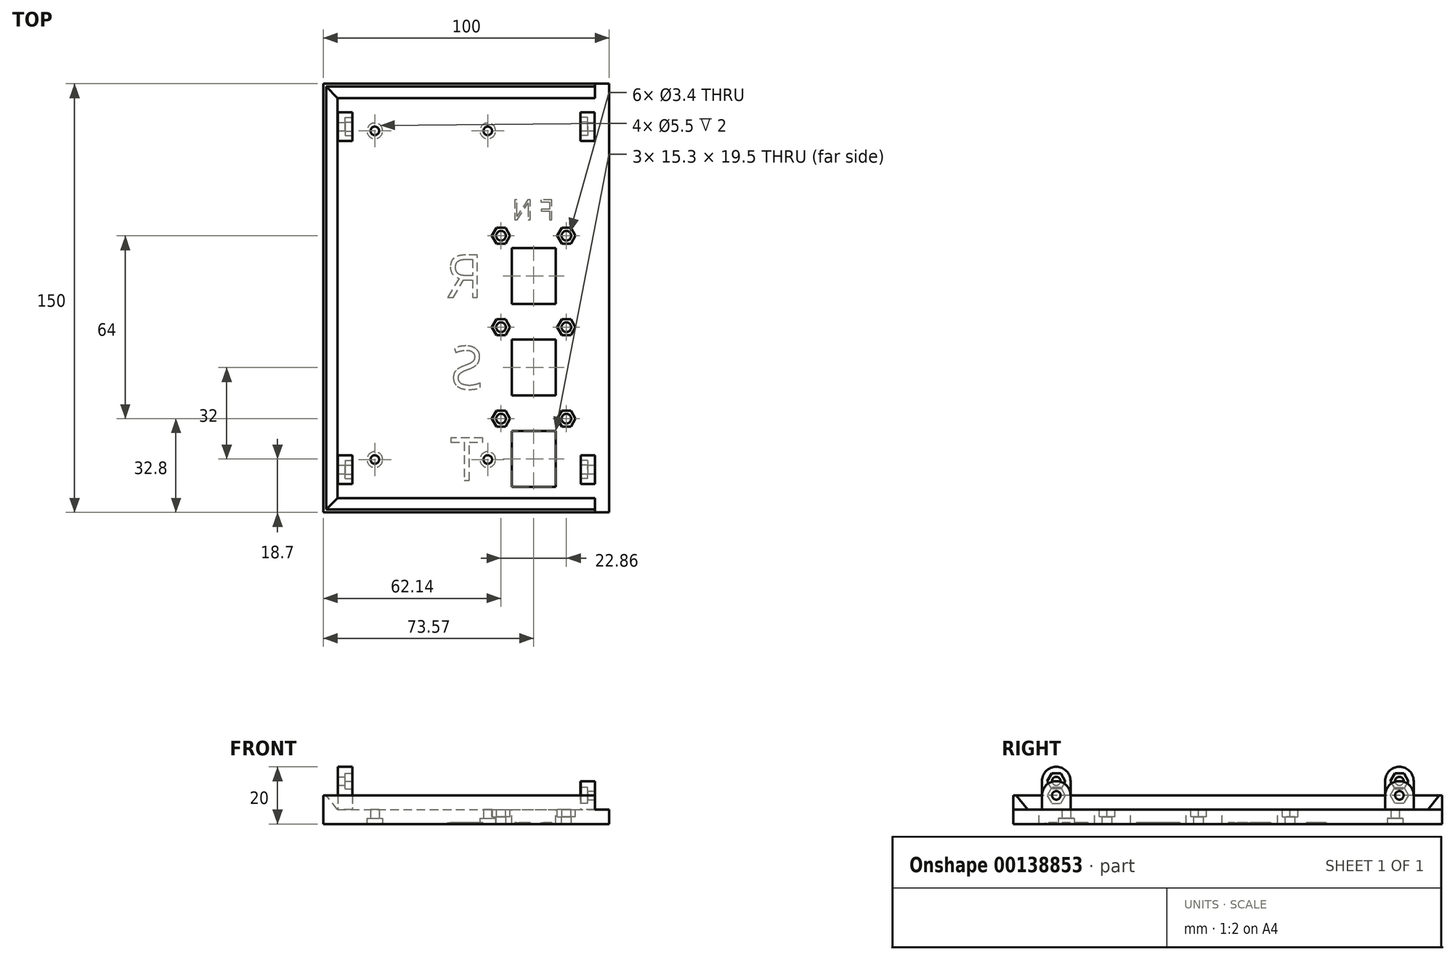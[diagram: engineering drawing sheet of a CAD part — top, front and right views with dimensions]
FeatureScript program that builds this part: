
annotation { "Feature Type Name" : "Feature", "Feature Type Description" : "" }
export const myFeature = defineFeature(function(context is Context, id is Id, definition is map)
    precondition{}
    {
        {
            var Q0;
            Q0=qCreatedBy(makeId("Top.planeOp"),FACE);
            var sketch = newSketch(context, id + "F0", { "sketchPlane" : qUnion([Q0])});
            skLineSegment(sketch, "E0.bottom", {"start": v(50, 75) * mm, "end": v(-50, 75) * mm});
            skLineSegment(sketch, "E0.top", {"start": v(50, -75) * mm, "end": v(-50, -75) * mm});
            skLineSegment(sketch, "E0.left", {"start": v(50, 75) * mm, "end": v(50, -75) * mm});
            skLineSegment(sketch, "E0.right", {"start": v(-50, 75) * mm, "end": v(-50, -75) * mm});
            skPoint(sketch, "E0.middle", {"position": v(0, 0) * mm});
            skSolve(sketch);
        }
        {
            var Q0;
            Q0 = qSketchRegion(id + "F0", true);
            extrude(context, id + "F1", {"entities" : qUnion([Q0]), "depth" : 5 * mm});
        }
        {
            var Q0;
            Q0=makeQuery(id+"F1.opExtrude","CAP_FACE",FACE,{"disambiguationData":[OSD([sQuery(id+"F0.wireOp",EDGE,"E0.bottom"),sQuery(id+"F0.wireOp",EDGE,"E0.top"),sQuery(id+"F0.wireOp",EDGE,"E0.left"),sQuery(id+"F0.wireOp",EDGE,"E0.right")])],"isStart":false});
            var sketch = newSketch(context, id + "F2", { "sketchPlane" : qUnion([Q0])});
            skLineSegment(sketch, "E1.bottom", {"start": v(-50, 75) * mm, "end": v(50, 75) * mm});
            skLineSegment(sketch, "E1.top", {"start": v(-50, -75) * mm, "end": v(50, -75) * mm});
            skLineSegment(sketch, "E1.left", {"start": v(-50, 75) * mm, "end": v(-50, -75) * mm});
            skLineSegment(sketch, "E1.right", {"start": v(50, 75) * mm, "end": v(50, -75) * mm});
            skLineSegment(sketch, "E2.bottom", {"start": v(-45, 70) * mm, "end": v(45, 70) * mm});
            skLineSegment(sketch, "E2.top", {"start": v(-45, -70) * mm, "end": v(45, -70) * mm});
            skLineSegment(sketch, "E2.left", {"start": v(-45, 70) * mm, "end": v(-45, -70) * mm});
            skLineSegment(sketch, "E2.right", {"start": v(45, 70) * mm, "end": v(45, -70) * mm});
            skLineSegment(sketch, "E3", {"start": v(45, 70) * mm, "end": v(45, 75) * mm});
            skLineSegment(sketch, "E4", {"start": v(45, -70) * mm, "end": v(45, -75) * mm});
            skSolve(sketch);
        }
        {
            var Q0;
            Q0=makeQuery(id+"FjEDbnMBrPMrPUJ_1.boolean.opBoolean","MERGE",FACE,{"derivedFrom":[makeQuery(id+"F1.opExtrude","SWEPT_FACE",FACE,{"disambiguationData":[OSD([sQuery(id+"F0.wireOp",EDGE,"E0.top")])]}),makeQuery(id+"FjEDbnMBrPMrPUJ_1.opExtrude","SWEPT_FACE",FACE,{"disambiguationData":[OSD([sQuery(id+"F2.wireOp",EDGE,"E1.top")])]})]});
            var sketch = newSketch(context, id + "F3", { "sketchPlane" : qUnion([Q0])});
            skLineSegment(sketch, "E5", {"start": v(-50, 0) * mm, "end": v(-50, 10) * mm});
            skLineSegment(sketch, "E6", {"start": v(-50, 10) * mm, "end": v(-49, 10) * mm});
            skLineSegment(sketch, "E7", {"start": v(-50, 5) * mm, "end": v(-45, 5) * mm});
            skLineSegment(sketch, "E8", {"start": v(-49, 10) * mm, "end": v(-45, 5) * mm});
            skSolve(sketch);
        }
        {
            var Q0;
            Q0=makeQuery(id+"F1.opExtrude","SWEPT_FACE",FACE,{"disambiguationData":[OSD([sQuery(id+"F0.wireOp",EDGE,"E0.left")])]});
            var sketch = newSketch(context, id + "F4", { "sketchPlane" : qUnion([Q0])});
            skLineSegment(sketch, "E9", {"start": v(-75, 0) * mm, "end": v(-75, 10) * mm});
            skLineSegment(sketch, "E10", {"start": v(-75, 5) * mm, "end": v(-70, 5) * mm});
            skLineSegment(sketch, "E11", {"start": v(-75, 10) * mm, "end": v(-74, 10) * mm});
            skLineSegment(sketch, "E12", {"start": v(-74, 10) * mm, "end": v(-70, 5) * mm});
            skLineSegment(sketch, "E13.MirrorCS", {"start": v(75, 10) * mm, "end": v(74, 10) * mm});
            skLineSegment(sketch, "E14.MirrorCS", {"start": v(75, 0) * mm, "end": v(75, 10) * mm});
            skLineSegment(sketch, "E15.MirrorCS", {"start": v(75, 5) * mm, "end": v(70, 5) * mm});
            skLineSegment(sketch, "E16.MirrorCS", {"start": v(74, 10) * mm, "end": v(70, 5) * mm});
            skSolve(sketch);
        }
        {
            var Q0;
            Q0 = qSketchRegion(id + "F3", true);
            extrude(context, id + "F5", {"entities" : qUnion([Q0]), "operationType" : NewBodyOperationType.ADD, "oppositeDirection" : true, "depth" : 150 * mm});
        }
        {
            var Q0;
            Q0 = qSketchRegion(id + "F4", true);
            extrude(context, id + "F6", {"entities" : qUnion([Q0]), "operationType" : NewBodyOperationType.ADD, "oppositeDirection" : true, "depth" : 100 * mm});
        }
        {
            var Q0;
            Q0=makeQuery(id+"F6.boolean.opBoolean","MERGE",FACE,{"derivedFrom":[makeQuery(id+"F5.boolean.opBoolean","MERGE",FACE,{"derivedFrom":[makeQuery(id+"F1.opExtrude","SWEPT_FACE",FACE,{"disambiguationData":[OSD([sQuery(id+"F0.wireOp",EDGE,"E0.top")])]}),makeQuery(id+"F5.opExtrude","CAP_FACE",FACE,{"disambiguationData":[OSD([sQuery(id+"F3.wireOp",EDGE,"E5"),sQuery(id+"F3.wireOp",EDGE,"E6"),sQuery(id+"F3.wireOp",EDGE,"E7"),sQuery(id+"F3.wireOp",EDGE,"E8")])],"isStart":true})]}),makeQuery(id+"F6.opExtrude","SWEPT_FACE",FACE,{"disambiguationData":[OSD([sQuery(id+"F4.wireOp",EDGE,"E9")])]})]});
            var sketch = newSketch(context, id + "F7", { "sketchPlane" : qUnion([Q0])});
            skLineSegment(sketch, "E17.bottom", {"start": v(50, 10) * mm, "end": v(45, 10) * mm});
            skLineSegment(sketch, "E17.top", {"start": v(50, 5) * mm, "end": v(45, 5) * mm});
            skLineSegment(sketch, "E17.left", {"start": v(50, 10) * mm, "end": v(50, 5) * mm});
            skLineSegment(sketch, "E17.right", {"start": v(45, 10) * mm, "end": v(45, 5) * mm});
            skSolve(sketch);
        }
        {
            var Q0;
            Q0 = qSketchRegion(id + "F7", true);
            extrude(context, id + "F8", {"entities" : qUnion([Q0]), "operationType" : NewBodyOperationType.REMOVE, "oppositeDirection" : true, "depth" : 160 * mm});
        }
        {
            var Q0;
            Q0=makeQuery(id+"F8.boolean.opBoolean","MERGE",FACE,{"derivedFrom":[makeQuery(id+"F1.opExtrude","CAP_FACE",FACE,{"disambiguationData":[OSD([sQuery(id+"F0.wireOp",EDGE,"E0.bottom"),sQuery(id+"F0.wireOp",EDGE,"E0.top"),sQuery(id+"F0.wireOp",EDGE,"E0.left"),sQuery(id+"F0.wireOp",EDGE,"E0.right")])],"isStart":false}),makeQuery(id+"F8.opExtrude","SWEPT_FACE",FACE,{"disambiguationData":[OSD([sQuery(id+"F7.wireOp",EDGE,"E17.top")])]})]});
            var sketch = newSketch(context, id + "F9", { "sketchPlane" : qUnion([Q0])});
            skLineSegment(sketch, "E18.bottom", {"start": v(15.92, 17.45) * mm, "end": v(31.22, 17.45) * mm});
            skLineSegment(sketch, "E18.top", {"start": v(15.92, -2.05) * mm, "end": v(31.22, -2.05) * mm});
            skLineSegment(sketch, "E18.left", {"start": v(15.92, 17.45) * mm, "end": v(15.92, -2.05) * mm});
            skLineSegment(sketch, "E18.right", {"start": v(31.22, 17.45) * mm, "end": v(31.22, -2.05) * mm});
            skLineSegment(sketch, "E19.bottom", {"start": v(5.14, 26) * mm, "end": v(42, 26) * mm});
            skLineSegment(sketch, "E19.left", {"start": v(5.14, 26) * mm, "end": v(5.14, -4.5) * mm});
            skLineSegment(sketch, "E19.right", {"start": v(42, 26) * mm, "end": v(42, -4.5) * mm});
            skCircle(sketch, "E20", {"center": v(12.14, 21.8) * mm, "radius": 1.7 * mm});
            skCircle(sketch, "E21", {"center": v(35, 21.8) * mm, "radius": 1.7 * mm});
            skLineSegment(sketch, "E22", {"start": v(5.14, -4.5) * mm, "end": v(42, -4.5) * mm});
            skLineSegment(sketch, "E23.0.1.0", {"start": v(5.14, -6) * mm, "end": v(42, -6) * mm});
            skLineSegment(sketch, "E23.0.1.1", {"start": v(15.92, -14.55) * mm, "end": v(31.22, -14.55) * mm});
            skLineSegment(sketch, "E23.0.1.2", {"start": v(5.14, -36.5) * mm, "end": v(42, -36.5) * mm});
            skLineSegment(sketch, "E23.0.1.3", {"start": v(31.22, -14.55) * mm, "end": v(31.22, -34.05) * mm});
            skLineSegment(sketch, "E23.0.1.4", {"start": v(42, -6) * mm, "end": v(42, -36.5) * mm});
            skLineSegment(sketch, "E23.0.1.5", {"start": v(15.92, -14.55) * mm, "end": v(15.92, -34.05) * mm});
            skLineSegment(sketch, "E23.0.1.6", {"start": v(5.14, -6) * mm, "end": v(5.14, -36.5) * mm});
            skLineSegment(sketch, "E23.0.1.7", {"start": v(15.92, -34.05) * mm, "end": v(31.22, -34.05) * mm});
            skCircle(sketch, "E23.0.1.8", {"center": v(35, -10.2) * mm, "radius": 1.7 * mm});
            skCircle(sketch, "E23.0.1.9", {"center": v(12.14, -10.2) * mm, "radius": 1.7 * mm});
            skLineSegment(sketch, "E23.0.2.0", {"start": v(5.14, -38) * mm, "end": v(42, -38) * mm});
            skLineSegment(sketch, "E23.0.2.1", {"start": v(15.92, -46.55) * mm, "end": v(31.22, -46.55) * mm});
            skLineSegment(sketch, "E23.0.2.2", {"start": v(5.14, -68.5) * mm, "end": v(42, -68.5) * mm});
            skLineSegment(sketch, "E23.0.2.3", {"start": v(31.22, -46.55) * mm, "end": v(31.22, -66.05) * mm});
            skLineSegment(sketch, "E23.0.2.4", {"start": v(42, -38) * mm, "end": v(42, -68.5) * mm});
            skLineSegment(sketch, "E23.0.2.5", {"start": v(15.92, -46.55) * mm, "end": v(15.92, -66.05) * mm});
            skLineSegment(sketch, "E23.0.2.6", {"start": v(5.14, -38) * mm, "end": v(5.14, -68.5) * mm});
            skLineSegment(sketch, "E23.0.2.7", {"start": v(15.92, -66.05) * mm, "end": v(31.22, -66.05) * mm});
            skCircle(sketch, "E23.0.2.8", {"center": v(35, -42.2) * mm, "radius": 1.7 * mm});
            skCircle(sketch, "E23.0.2.9", {"center": v(12.14, -42.2) * mm, "radius": 1.7 * mm});
            skLineSegment(sketch, "E23.direction1", {"start": v(5.14, -4.5) * mm, "end": v(42, -4.5) * mm, "construction": true});
            skLineSegment(sketch, "E23.direction2", {"start": v(5.14, -4.5) * mm, "end": v(5.14, -36.5) * mm, "construction": true});
            skSolve(sketch);
        }
        {
            var Q0;
            Q0=makeQuery(id+"F1.opExtrude","CAP_FACE",FACE,{"disambiguationData":[OSD([sQuery(id+"F0.wireOp",EDGE,"E0.bottom"),sQuery(id+"F0.wireOp",EDGE,"E0.top"),sQuery(id+"F0.wireOp",EDGE,"E0.left"),sQuery(id+"F0.wireOp",EDGE,"E0.right")])],"isStart":true});
            var sketch = newSketch(context, id + "F10", { "sketchPlane" : qUnion([Q0])});
            skCircle(sketch, "E24", {"center": v(7.5, 56.5) * mm, "radius": 1.5 * mm});
            skCircle(sketch, "E25", {"center": v(-32, -58.5) * mm, "radius": 1.5 * mm});
            skCircle(sketch, "E26", {"center": v(7.5, -58.5) * mm, "radius": 1.5 * mm});
            skCircle(sketch, "E27", {"center": v(-32, 56.5) * mm, "radius": 1.5 * mm});
            skSolve(sketch);
        }
        {
            var Q0;
            Q0 = qSketchRegion(id + "F10", true);
            extrude(context, id + "F11", {"entities" : qUnion([Q0]), "operationType" : NewBodyOperationType.REMOVE, "oppositeDirection" : true, "depth" : 25 * mm});
        }
        {
            var Q0;
            Q0=makeQuery(id+"F1.opExtrude","CAP_FACE",FACE,{"disambiguationData":[OSD([sQuery(id+"F0.wireOp",EDGE,"E0.bottom"),sQuery(id+"F0.wireOp",EDGE,"E0.top"),sQuery(id+"F0.wireOp",EDGE,"E0.left"),sQuery(id+"F0.wireOp",EDGE,"E0.right")])],"isStart":true});
            var sketch = newSketch(context, id + "F12", { "sketchPlane" : qUnion([Q0])});
            skCircle(sketch, "E28", {"center": v(-32, 56.5) * mm, "radius": 2.75 * mm});
            skCircle(sketch, "E29", {"center": v(7.5, 56.5) * mm, "radius": 2.75 * mm});
            skCircle(sketch, "E30", {"center": v(-32, -58.5) * mm, "radius": 2.75 * mm});
            skCircle(sketch, "E31", {"center": v(7.5, -58.5) * mm, "radius": 2.75 * mm});
            skSolve(sketch);
        }
        {
            var Q0;
            Q0 = qSketchRegion(id + "F12", true);
            extrude(context, id + "F13", {"entities" : qUnion([Q0]), "operationType" : NewBodyOperationType.REMOVE, "oppositeDirection" : true, "depth" : 2 * mm});
        }
        {
            var Q0;
            Q0=makeQuery(id+"F8.boolean.opBoolean","MERGE",FACE,{"derivedFrom":[makeQuery(id+"F1.opExtrude","CAP_FACE",FACE,{"disambiguationData":[OSD([sQuery(id+"F0.wireOp",EDGE,"E0.bottom"),sQuery(id+"F0.wireOp",EDGE,"E0.top"),sQuery(id+"F0.wireOp",EDGE,"E0.left"),sQuery(id+"F0.wireOp",EDGE,"E0.right")])],"isStart":false}),makeQuery(id+"F8.opExtrude","SWEPT_FACE",FACE,{"disambiguationData":[OSD([sQuery(id+"F7.wireOp",EDGE,"E17.top")])]})]});
            var sketch = newSketch(context, id + "F14", { "sketchPlane" : qUnion([Q0])});
            skLineSegment(sketch, "E32.bottom", {"start": v(-39.9, 65) * mm, "end": v(-44.9, 65) * mm});
            skLineSegment(sketch, "E32.top", {"start": v(-39.9, 55) * mm, "end": v(-44.9, 55) * mm});
            skLineSegment(sketch, "E32.left", {"start": v(-39.9, 65) * mm, "end": v(-39.9, 55) * mm});
            skLineSegment(sketch, "E32.right", {"start": v(-44.9, 65) * mm, "end": v(-44.9, 55) * mm});
            skLineSegment(sketch, "E33.bottom", {"start": v(44.9, 65) * mm, "end": v(39.9, 65) * mm});
            skLineSegment(sketch, "E33.top", {"start": v(44.9, 55) * mm, "end": v(39.9, 55) * mm});
            skLineSegment(sketch, "E33.left", {"start": v(44.9, 65) * mm, "end": v(44.9, 55) * mm});
            skLineSegment(sketch, "E33.right", {"start": v(39.9, 65) * mm, "end": v(39.9, 55) * mm});
            skLineSegment(sketch, "E34.bottom", {"start": v(-39.9, -55) * mm, "end": v(-44.9, -55) * mm});
            skLineSegment(sketch, "E34.top", {"start": v(-39.9, -65) * mm, "end": v(-44.9, -65) * mm});
            skLineSegment(sketch, "E34.left", {"start": v(-39.9, -55) * mm, "end": v(-39.9, -65) * mm});
            skLineSegment(sketch, "E34.right", {"start": v(-44.9, -55) * mm, "end": v(-44.9, -65) * mm});
            skLineSegment(sketch, "E35.bottom", {"start": v(45, -55) * mm, "end": v(40, -55) * mm});
            skLineSegment(sketch, "E35.top", {"start": v(45, -65) * mm, "end": v(40, -65) * mm});
            skLineSegment(sketch, "E35.left", {"start": v(45, -55) * mm, "end": v(45, -65) * mm});
            skLineSegment(sketch, "E35.right", {"start": v(40, -55) * mm, "end": v(40, -65) * mm});
            skSolve(sketch);
        }
        {
            var Q0;
            Q0 = qSketchRegion(id + "F14", true);
            extrude(context, id + "F15", {"entities" : qUnion([Q0]), "operationType" : NewBodyOperationType.ADD, "depth" : 20 * mm});
        }
        {
            var Q0;
            Q0=makeQuery(id+"F15.opExtrude","SWEPT_FACE",FACE,{"disambiguationData":[OSD([sQuery(id+"F14.wireOp",EDGE,"E35.left")])]});
            var sketch = newSketch(context, id + "F16", { "sketchPlane" : qUnion([Q0])});
            skCircle(sketch, "E36", {"center": v(-60, 10) * mm, "radius": 1.5 * mm});
            skLineSegment(sketch, "E37", {"start": v(-65, 10) * mm, "end": v(-65, 25) * mm});
            skLineSegment(sketch, "E38", {"start": v(-65, 25) * mm, "end": v(-55, 25) * mm});
            skLineSegment(sketch, "E39", {"start": v(-55, 25) * mm, "end": v(-55, 10) * mm});
            skArc(sketch, "E40", {"start": v(-55, 10) * mm, "mid": v(-60, 15) * mm, "end": v(-65, 10) * mm});
            skCircle(sketch, "E41.MirrorC", {"center": v(60, 10) * mm, "radius": 1.5 * mm});
            skLineSegment(sketch, "E42.MirrorCS", {"start": v(55, 25) * mm, "end": v(55, 10) * mm});
            skLineSegment(sketch, "E43.MirrorCS", {"start": v(65, 10) * mm, "end": v(65, 25) * mm});
            skArc(sketch, "E44.MirrorCS", {"start": v(55, 10) * mm, "mid": v(60, 15) * mm, "end": v(65, 10) * mm});
            skLineSegment(sketch, "E45.MirrorCS", {"start": v(65, 25) * mm, "end": v(55, 25) * mm});
            skSolve(sketch);
        }
        {
            var Q0;
            Q0 = qSketchRegion(id + "F16", true);
            extrude(context, id + "F17", {"entities" : qUnion([Q0]), "operationType" : NewBodyOperationType.REMOVE, "oppositeDirection" : true, "depth" : 10 * mm});
        }
        {
            var Q0;
            Q0=makeQuery(id+"F15.opExtrude","SWEPT_FACE",FACE,{"disambiguationData":[OSD([sQuery(id+"F14.wireOp",EDGE,"E34.left")])]});
            var sketch = newSketch(context, id + "F18", { "sketchPlane" : qUnion([Q0])});
            skCircle(sketch, "E46", {"center": v(-60, 15) * mm, "radius": 1.5 * mm});
            skArc(sketch, "E47", {"start": v(-55, 15) * mm, "mid": v(-60, 20) * mm, "end": v(-65, 15) * mm});
            skLineSegment(sketch, "E48", {"start": v(-55, 15) * mm, "end": v(-55, 25) * mm});
            skLineSegment(sketch, "E49", {"start": v(-55, 25) * mm, "end": v(-65, 25) * mm});
            skLineSegment(sketch, "E50", {"start": v(-65, 25) * mm, "end": v(-65, 15) * mm});
            skLineSegment(sketch, "E51.MirrorCS", {"start": v(55, 15) * mm, "end": v(55, 25) * mm});
            skLineSegment(sketch, "E52.MirrorCS", {"start": v(55, 25) * mm, "end": v(65, 25) * mm});
            skArc(sketch, "E53.MirrorCS", {"start": v(55, 15) * mm, "mid": v(60, 20) * mm, "end": v(65, 15) * mm});
            skLineSegment(sketch, "E54.MirrorCS", {"start": v(65, 25) * mm, "end": v(65, 15) * mm});
            skCircle(sketch, "E55.MirrorC", {"center": v(60, 15) * mm, "radius": 1.5 * mm});
            skSolve(sketch);
        }
        {
            var Q0;
            Q0 = qSketchRegion(id + "F18", true);
            extrude(context, id + "F19", {"entities" : qUnion([Q0]), "operationType" : NewBodyOperationType.REMOVE, "oppositeDirection" : true, "depth" : 25 * mm});
        }
        {
            var Q0;
            Q0=makeQuery(id+"F15.opExtrude","SWEPT_FACE",FACE,{"disambiguationData":[OSD([sQuery(id+"F14.wireOp",EDGE,"E35.right")])]});
            var sketch = newSketch(context, id + "F20", { "sketchPlane" : qUnion([Q0])});
            skCircle(sketch, "E56.cCircle", {"center": v(60, 10) * mm, "radius": 2.75 * mm, "construction": true});
            skLineSegment(sketch, "E56.0", {"start": v(58.41, 12.75) * mm, "end": v(61.59, 12.75) * mm});
            skLineSegment(sketch, "E56.1", {"start": v(61.59, 12.75) * mm, "end": v(63.18, 10) * mm});
            skLineSegment(sketch, "E56.2", {"start": v(63.18, 10) * mm, "end": v(61.59, 7.25) * mm});
            skLineSegment(sketch, "E56.3", {"start": v(61.59, 7.25) * mm, "end": v(58.41, 7.25) * mm});
            skLineSegment(sketch, "E56.4", {"start": v(58.41, 7.25) * mm, "end": v(56.82, 10) * mm});
            skLineSegment(sketch, "E56.5", {"start": v(56.82, 10) * mm, "end": v(58.41, 12.75) * mm});
            skPoint(sketch, "E56.0.midPoint", {"position": v(60, 12.75) * mm});
            skLineSegment(sketch, "E57.MirrorCS", {"start": v(-56.82, 10) * mm, "end": v(-58.41, 12.75) * mm});
            skLineSegment(sketch, "E58.MirrorCS", {"start": v(-58.41, 7.25) * mm, "end": v(-56.82, 10) * mm});
            skLineSegment(sketch, "E59.MirrorCS", {"start": v(-61.59, 7.25) * mm, "end": v(-58.41, 7.25) * mm});
            skLineSegment(sketch, "E60.MirrorCS", {"start": v(-63.18, 10) * mm, "end": v(-61.59, 7.25) * mm});
            skLineSegment(sketch, "E61.MirrorCS", {"start": v(-61.59, 12.75) * mm, "end": v(-63.18, 10) * mm});
            skLineSegment(sketch, "E62.MirrorCS", {"start": v(-58.41, 12.75) * mm, "end": v(-61.59, 12.75) * mm});
            skCircle(sketch, "E63.MirrorC", {"center": v(-60, 10) * mm, "radius": 2.75 * mm, "construction": true});
            skPoint(sketch, "E64.MirrorP", {"position": v(-60, 12.75) * mm});
            skSolve(sketch);
        }
        {
            var Q0;
            Q0 = qSketchRegion(id + "F20", true);
            extrude(context, id + "F21", {"entities" : qUnion([Q0]), "operationType" : NewBodyOperationType.REMOVE, "oppositeDirection" : true, "depth" : 2.5 * mm});
        }
        {
            var Q0;
            Q0=makeQuery(id+"F15.opExtrude","SWEPT_FACE",FACE,{"disambiguationData":[OSD([sQuery(id+"F14.wireOp",EDGE,"E34.left")])]});
            var sketch = newSketch(context, id + "F22", { "sketchPlane" : qUnion([Q0])});
            skCircle(sketch, "E65.cCircle", {"center": v(-60, 15) * mm, "radius": 2.75 * mm, "construction": true});
            skLineSegment(sketch, "E65.0", {"start": v(-61.59, 17.75) * mm, "end": v(-58.41, 17.75) * mm});
            skLineSegment(sketch, "E65.1", {"start": v(-58.41, 17.75) * mm, "end": v(-56.82, 15) * mm});
            skLineSegment(sketch, "E65.2", {"start": v(-56.82, 15) * mm, "end": v(-58.41, 12.25) * mm});
            skLineSegment(sketch, "E65.3", {"start": v(-58.41, 12.25) * mm, "end": v(-61.59, 12.25) * mm});
            skLineSegment(sketch, "E65.4", {"start": v(-61.59, 12.25) * mm, "end": v(-63.18, 15) * mm});
            skLineSegment(sketch, "E65.5", {"start": v(-63.18, 15) * mm, "end": v(-61.59, 17.75) * mm});
            skPoint(sketch, "E65.0.midPoint", {"position": v(-60, 17.75) * mm});
            skLineSegment(sketch, "E66.MirrorCS", {"start": v(63.18, 15) * mm, "end": v(61.59, 17.75) * mm});
            skLineSegment(sketch, "E67.MirrorCS", {"start": v(58.41, 12.25) * mm, "end": v(61.59, 12.25) * mm});
            skLineSegment(sketch, "E68.MirrorCS", {"start": v(61.59, 17.75) * mm, "end": v(58.41, 17.75) * mm});
            skLineSegment(sketch, "E69.MirrorCS", {"start": v(61.59, 12.25) * mm, "end": v(63.18, 15) * mm});
            skLineSegment(sketch, "E70.MirrorCS", {"start": v(56.82, 15) * mm, "end": v(58.41, 12.25) * mm});
            skLineSegment(sketch, "E71.MirrorCS", {"start": v(58.41, 17.75) * mm, "end": v(56.82, 15) * mm});
            skCircle(sketch, "E72.MirrorC", {"center": v(60, 15) * mm, "radius": 2.75 * mm, "construction": true});
            skPoint(sketch, "E73.MirrorP", {"position": v(60, 17.75) * mm});
            skSolve(sketch);
        }
        {
            var Q0;
            Q0 = qSketchRegion(id + "F22", true);
            extrude(context, id + "F23", {"entities" : qUnion([Q0]), "operationType" : NewBodyOperationType.REMOVE, "oppositeDirection" : true, "depth" : 2.5 * mm});
        }
        {
            var Q0;
            Q0=makeQuery(id+"F8.boolean.opBoolean","MERGE",FACE,{"derivedFrom":[makeQuery(id+"F1.opExtrude","CAP_FACE",FACE,{"disambiguationData":[OSD([sQuery(id+"F0.wireOp",EDGE,"E0.bottom"),sQuery(id+"F0.wireOp",EDGE,"E0.top"),sQuery(id+"F0.wireOp",EDGE,"E0.left"),sQuery(id+"F0.wireOp",EDGE,"E0.right")])],"isStart":false}),makeQuery(id+"F8.opExtrude","SWEPT_FACE",FACE,{"disambiguationData":[OSD([sQuery(id+"F7.wireOp",EDGE,"E17.top")])]})]});
            var sketch = newSketch(context, id + "F24", { "sketchPlane" : qUnion([Q0])});
            skCircle(sketch, "E74.cCircle", {"center": v(12.14, 21.8) * mm, "radius": 2.75 * mm, "construction": true});
            skLineSegment(sketch, "E74.0", {"start": v(10.55, 24.55) * mm, "end": v(13.73, 24.55) * mm});
            skLineSegment(sketch, "E74.1", {"start": v(13.73, 24.55) * mm, "end": v(15.32, 21.8) * mm});
            skLineSegment(sketch, "E74.2", {"start": v(15.32, 21.8) * mm, "end": v(13.73, 19.05) * mm});
            skLineSegment(sketch, "E74.3", {"start": v(13.73, 19.05) * mm, "end": v(10.55, 19.05) * mm});
            skLineSegment(sketch, "E74.4", {"start": v(10.55, 19.05) * mm, "end": v(8.96, 21.8) * mm});
            skLineSegment(sketch, "E74.5", {"start": v(8.96, 21.8) * mm, "end": v(10.55, 24.55) * mm});
            skPoint(sketch, "E74.0.midPoint", {"position": v(12.14, 24.55) * mm});
            skPoint(sketch, "E75.0.1.0", {"position": v(12.14, -7.45) * mm});
            skLineSegment(sketch, "E75.0.1.1", {"start": v(13.73, -7.45) * mm, "end": v(15.32, -10.2) * mm});
            skLineSegment(sketch, "E75.0.1.2", {"start": v(15.32, -10.2) * mm, "end": v(13.73, -12.95) * mm});
            skCircle(sketch, "E75.0.1.3", {"center": v(12.14, -10.2) * mm, "radius": 2.75 * mm, "construction": true});
            skLineSegment(sketch, "E75.0.1.4", {"start": v(10.55, -7.45) * mm, "end": v(13.73, -7.45) * mm});
            skLineSegment(sketch, "E75.0.1.5", {"start": v(10.55, -12.95) * mm, "end": v(8.96, -10.2) * mm});
            skLineSegment(sketch, "E75.0.1.6", {"start": v(13.73, -12.95) * mm, "end": v(10.55, -12.95) * mm});
            skLineSegment(sketch, "E75.0.1.7", {"start": v(8.96, -10.2) * mm, "end": v(10.55, -7.45) * mm});
            skPoint(sketch, "E75.0.2.0", {"position": v(12.14, -39.45) * mm});
            skLineSegment(sketch, "E75.0.2.1", {"start": v(13.73, -39.45) * mm, "end": v(15.32, -42.2) * mm});
            skLineSegment(sketch, "E75.0.2.2", {"start": v(15.32, -42.2) * mm, "end": v(13.73, -44.95) * mm});
            skCircle(sketch, "E75.0.2.3", {"center": v(12.14, -42.2) * mm, "radius": 2.75 * mm, "construction": true});
            skLineSegment(sketch, "E75.0.2.4", {"start": v(10.55, -39.45) * mm, "end": v(13.73, -39.45) * mm});
            skLineSegment(sketch, "E75.0.2.5", {"start": v(10.55, -44.95) * mm, "end": v(8.96, -42.2) * mm});
            skLineSegment(sketch, "E75.0.2.6", {"start": v(13.73, -44.95) * mm, "end": v(10.55, -44.95) * mm});
            skLineSegment(sketch, "E75.0.2.7", {"start": v(8.96, -42.2) * mm, "end": v(10.55, -39.45) * mm});
            skPoint(sketch, "E75.1.0.0", {"position": v(35, 24.55) * mm});
            skLineSegment(sketch, "E75.1.0.1", {"start": v(36.59, 24.55) * mm, "end": v(38.18, 21.8) * mm});
            skLineSegment(sketch, "E75.1.0.2", {"start": v(38.18, 21.8) * mm, "end": v(36.59, 19.05) * mm});
            skCircle(sketch, "E75.1.0.3", {"center": v(35, 21.8) * mm, "radius": 2.75 * mm, "construction": true});
            skLineSegment(sketch, "E75.1.0.4", {"start": v(33.41, 24.55) * mm, "end": v(36.59, 24.55) * mm});
            skLineSegment(sketch, "E75.1.0.5", {"start": v(33.41, 19.05) * mm, "end": v(31.82, 21.8) * mm});
            skLineSegment(sketch, "E75.1.0.6", {"start": v(36.59, 19.05) * mm, "end": v(33.41, 19.05) * mm});
            skLineSegment(sketch, "E75.1.0.7", {"start": v(31.82, 21.8) * mm, "end": v(33.41, 24.55) * mm});
            skPoint(sketch, "E75.1.1.0", {"position": v(35, -7.45) * mm});
            skLineSegment(sketch, "E75.1.1.1", {"start": v(36.59, -7.45) * mm, "end": v(38.18, -10.2) * mm});
            skLineSegment(sketch, "E75.1.1.2", {"start": v(38.18, -10.2) * mm, "end": v(36.59, -12.95) * mm});
            skCircle(sketch, "E75.1.1.3", {"center": v(35, -10.2) * mm, "radius": 2.75 * mm, "construction": true});
            skLineSegment(sketch, "E75.1.1.4", {"start": v(33.41, -7.45) * mm, "end": v(36.59, -7.45) * mm});
            skLineSegment(sketch, "E75.1.1.5", {"start": v(33.41, -12.95) * mm, "end": v(31.82, -10.2) * mm});
            skLineSegment(sketch, "E75.1.1.6", {"start": v(36.59, -12.95) * mm, "end": v(33.41, -12.95) * mm});
            skLineSegment(sketch, "E75.1.1.7", {"start": v(31.82, -10.2) * mm, "end": v(33.41, -7.45) * mm});
            skPoint(sketch, "E75.1.2.0", {"position": v(35, -39.45) * mm});
            skLineSegment(sketch, "E75.1.2.1", {"start": v(36.59, -39.45) * mm, "end": v(38.18, -42.2) * mm});
            skLineSegment(sketch, "E75.1.2.2", {"start": v(38.18, -42.2) * mm, "end": v(36.59, -44.95) * mm});
            skCircle(sketch, "E75.1.2.3", {"center": v(35, -42.2) * mm, "radius": 2.75 * mm, "construction": true});
            skLineSegment(sketch, "E75.1.2.4", {"start": v(33.41, -39.45) * mm, "end": v(36.59, -39.45) * mm});
            skLineSegment(sketch, "E75.1.2.5", {"start": v(33.41, -44.95) * mm, "end": v(31.82, -42.2) * mm});
            skLineSegment(sketch, "E75.1.2.6", {"start": v(36.59, -44.95) * mm, "end": v(33.41, -44.95) * mm});
            skLineSegment(sketch, "E75.1.2.7", {"start": v(31.82, -42.2) * mm, "end": v(33.41, -39.45) * mm});
            skLineSegment(sketch, "E75.direction1", {"start": v(10.55, 19.05) * mm, "end": v(33.41, 19.05) * mm, "construction": true});
            skLineSegment(sketch, "E75.direction2", {"start": v(10.55, 19.05) * mm, "end": v(10.55, -12.95) * mm, "construction": true});
            skSolve(sketch);
        }
        {
            var Q0;
            Q0 = qSketchRegion(id + "F24", true);
            extrude(context, id + "F25", {"entities" : qUnion([Q0]), "operationType" : NewBodyOperationType.REMOVE, "oppositeDirection" : true, "depth" : 2.5 * mm});
        }
        {
            var Q0;
            Q0=makeQuery(id+"F9.imprint","IMPRINT",FACE,{"disambiguationData":[TD([[makeQuery(id+"F9.imprint","IMPRINT",EDGE,{"derivedFrom":sQuery(id+"F9.wireOp",EDGE,"E21")}),1.0]])]});
            var Q1;
            Q1=makeQuery(id+"F9.imprint","IMPRINT",FACE,{"disambiguationData":[TD([[makeQuery(id+"F9.imprint","IMPRINT",EDGE,{"derivedFrom":sQuery(id+"F9.wireOp",EDGE,"E20")}),1.0]])]});
            var Q2;
            Q2=makeQuery(id+"F9.imprint","IMPRINT",FACE,{"disambiguationData":[TD([[makeQuery(id+"F9.imprint","IMPRINT",EDGE,{"derivedFrom":sQuery(id+"F9.wireOp",EDGE,"E18.bottom")}),-1.0]])]});
            var Q3;
            Q3=makeQuery(id+"F9.imprint","IMPRINT",FACE,{"disambiguationData":[TD([[makeQuery(id+"F9.imprint","IMPRINT",EDGE,{"derivedFrom":sQuery(id+"F9.wireOp",EDGE,"E23.0.1.8")}),1.0]])]});
            var Q4;
            Q4=makeQuery(id+"F9.imprint","IMPRINT",FACE,{"disambiguationData":[TD([[makeQuery(id+"F9.imprint","IMPRINT",EDGE,{"derivedFrom":sQuery(id+"F9.wireOp",EDGE,"E23.0.1.9")}),1.0]])]});
            var Q5;
            Q5=makeQuery(id+"F9.imprint","IMPRINT",FACE,{"disambiguationData":[TD([[makeQuery(id+"F9.imprint","IMPRINT",EDGE,{"derivedFrom":sQuery(id+"F9.wireOp",EDGE,"E23.0.1.1")}),-1.0]])]});
            var Q6;
            Q6=makeQuery(id+"F9.imprint","IMPRINT",FACE,{"disambiguationData":[TD([[makeQuery(id+"F9.imprint","IMPRINT",EDGE,{"derivedFrom":sQuery(id+"F9.wireOp",EDGE,"E23.0.2.8")}),1.0]])]});
            var Q7;
            Q7=makeQuery(id+"F9.imprint","IMPRINT",FACE,{"disambiguationData":[TD([[makeQuery(id+"F9.imprint","IMPRINT",EDGE,{"derivedFrom":sQuery(id+"F9.wireOp",EDGE,"E23.0.2.9")}),1.0]])]});
            var Q8;
            Q8=makeQuery(id+"F9.imprint","IMPRINT",FACE,{"disambiguationData":[TD([[makeQuery(id+"F9.imprint","IMPRINT",EDGE,{"derivedFrom":sQuery(id+"F9.wireOp",EDGE,"E23.0.2.1")}),-1.0]])]});
            extrude(context, id + "F26", {"entities" : qUnion([Q0, Q1, Q2, Q3, Q4, Q5, Q6, Q7, Q8]), "operationType" : NewBodyOperationType.REMOVE, "oppositeDirection" : true, "depth" : 25 * mm});
        }
        {
            var Q0;
            Q0=makeQuery(id+"F1.opExtrude","CAP_FACE",FACE,{"disambiguationData":[OSD([sQuery(id+"F0.wireOp",EDGE,"E0.bottom"),sQuery(id+"F0.wireOp",EDGE,"E0.top"),sQuery(id+"F0.wireOp",EDGE,"E0.left"),sQuery(id+"F0.wireOp",EDGE,"E0.right")])],"isStart":true});
            var sketch = newSketch(context, id + "F27", { "sketchPlane" : qUnion([Q0])});
            skText(sketch, "E76", { "text": "R", "fontName": "OpenSans-Regular.ttf"});
            skText(sketch, "E77", { "text": "S", "fontName": "OpenSans-Regular.ttf"});
            skText(sketch, "E78", { "text": "T", "fontName": "OpenSans-Regular.ttf"});
            skText(sketch, "E79", { "text": "F N", "fontName": "OpenSans-Regular.ttf"});
            const initialGuessF27  = {"E76": [0.00592, -0.0002, -1, 0, 0.015], "E77": [0.00592, 0.0318, -1, 0, 0.015], "E78": [0.00592, 0.0638, -1, 0, 0.015], "E79": [0.03086, -0.02745, -1, 0, 0.007]};
            skSetInitialGuess(sketch, initialGuessF27);
            skSolve(sketch);
        }
        {
            var Q0;
            Q0 = qSketchRegion(id + "F27", true);
            extrude(context, id + "F28", {"entities" : qUnion([Q0]), "operationType" : NewBodyOperationType.REMOVE, "oppositeDirection" : true, "depth" : 0.5 * mm});
        }
    });
